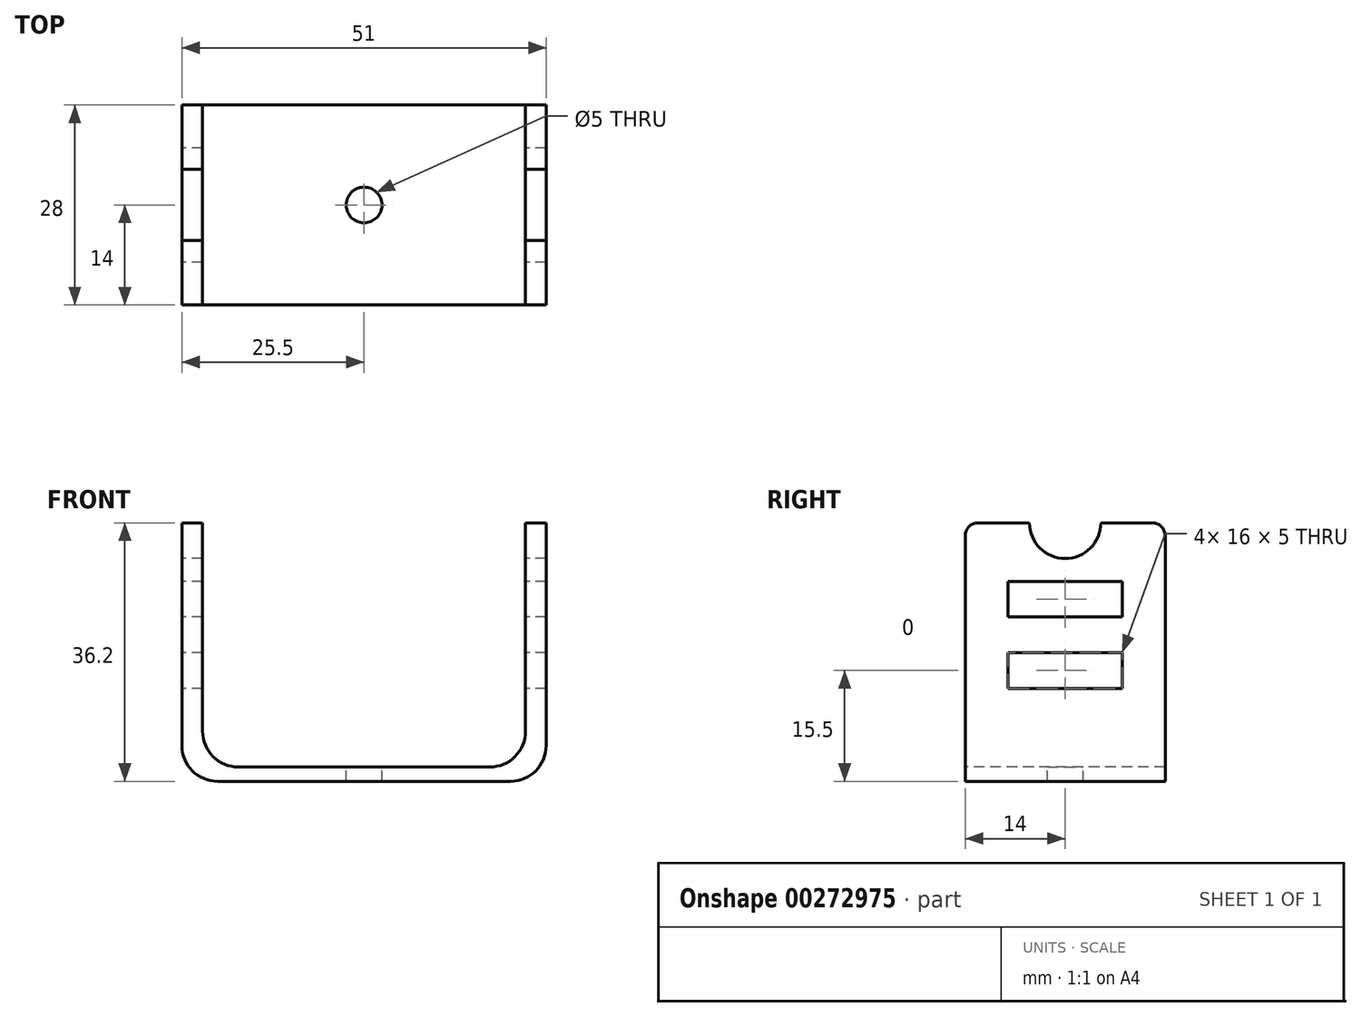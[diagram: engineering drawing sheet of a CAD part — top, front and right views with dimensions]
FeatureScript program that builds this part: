
annotation { "Feature Type Name" : "Feature", "Feature Type Description" : "" }
export const myFeature = defineFeature(function(context is Context, id is Id, definition is map)
    precondition{}
    {
        {
            var Q0;
            Q0=qCreatedBy(makeId("Right.planeOp"),FACE);
            var sketch = newSketch(context, id + "F0", { "sketchPlane" : qUnion([Q0])});
            skLineSegment(sketch, "E0.bottom", {"start": v(-14, 0) * mm, "end": v(14, 0) * mm});
            skLineSegment(sketch, "E0.top", {"start": v(-12.17, 36.2) * mm, "end": v(-5, 36.2) * mm});
            skLineSegment(sketch, "E0.left", {"start": v(-14, 0) * mm, "end": v(-14, 34.37) * mm});
            skLineSegment(sketch, "E0.right", {"start": v(14, 0) * mm, "end": v(14, 34.37) * mm});
            skLineSegment(sketch, "E1.bottom", {"start": v(-8, 18) * mm, "end": v(8, 18) * mm});
            skLineSegment(sketch, "E1.top", {"start": v(-8, 13) * mm, "end": v(8, 13) * mm});
            skLineSegment(sketch, "E1.left", {"start": v(-8, 18) * mm, "end": v(-8, 13) * mm});
            skLineSegment(sketch, "E1.right", {"start": v(8, 18) * mm, "end": v(8, 13) * mm});
            skLineSegment(sketch, "E2.0.1.0", {"start": v(-8, 23) * mm, "end": v(8, 23) * mm});
            skLineSegment(sketch, "E2.0.1.1", {"start": v(8, 28) * mm, "end": v(8, 23) * mm});
            skLineSegment(sketch, "E2.0.1.2", {"start": v(-8, 28) * mm, "end": v(8, 28) * mm});
            skLineSegment(sketch, "E2.0.1.3", {"start": v(-8, 28) * mm, "end": v(-8, 23) * mm});
            skLineSegment(sketch, "E2.direction1", {"start": v(-8, 13) * mm, "end": v(17, 13) * mm, "construction": true});
            skLineSegment(sketch, "E2.direction2", {"start": v(-8, 13) * mm, "end": v(-8, 23) * mm, "construction": true});
            skArc(sketch, "E3", {"start": v(-5, 36.2) * mm, "mid": v(0, 31.2) * mm, "end": v(5, 36.2) * mm});
            skLineSegment(sketch, "E4.trimOffspring", {"start": v(5, 36.2) * mm, "end": v(12.17, 36.2) * mm});
            skPoint(sketch, "E5.visualSharp", {"position": v(-14, 36.2) * mm});
            skArc(sketch, "E5.filletArc", {"start": v(-12.17, 36.2) * mm, "mid": v(-13.46, 35.66) * mm, "end": v(-14, 34.37) * mm});
            skPoint(sketch, "E6.visualSharp", {"position": v(14, 36.2) * mm});
            skArc(sketch, "E6.filletArc", {"start": v(14, 34.37) * mm, "mid": v(13.46, 35.66) * mm, "end": v(12.17, 36.2) * mm});
            skSolve(sketch);
        }
        {
            var Q0;
            Q0=makeQuery(id+"F0.imprint","IMPRINT",FACE,{"disambiguationData":[TD([[makeQuery(id+"F0.imprint","IMPRINT",EDGE,{"derivedFrom":sQuery(id+"F0.wireOp",EDGE,"E0.bottom")}),1.0]])]});
            extrude(context, id + "F1", {"entities" : qUnion([Q0]), "endBound" : BoundingType.SYMMETRIC, "depth" : 51 * mm});
        }
        {
            var Q0;
            Q0=makeQuery(id+"F1.opExtrude","SWEPT_FACE",FACE,{"disambiguationData":[OSD([sQuery(id+"F0.wireOp",EDGE,"E0.top")])]});
            var sketch = newSketch(context, id + "F2", { "sketchPlane" : qUnion([Q0])});
            skLineSegment(sketch, "E7.bottom", {"start": v(-22.6, 21.8) * mm, "end": v(22.6, 21.8) * mm});
            skLineSegment(sketch, "E7.top", {"start": v(-22.6, -21.02) * mm, "end": v(22.6, -21.02) * mm});
            skLineSegment(sketch, "E7.left", {"start": v(-22.6, 21.8) * mm, "end": v(-22.6, -21.02) * mm});
            skLineSegment(sketch, "E7.right", {"start": v(22.6, 21.8) * mm, "end": v(22.6, -21.02) * mm});
            skSolve(sketch);
        }
        {
            var Q0;
            Q0=qSketchRegion(id+"F2",true);
            extrude(context, id + "F3", {"entities" : qUnion([Q0]), "operationType" : NewBodyOperationType.REMOVE, "oppositeDirection" : true, "depth" : 34.2 * mm});
        }
        {
            var Q0;
            Q0=makeQuery(id+"F3.boolean.opBoolean","COPY",FACE,{"derivedFrom":makeQuery(id+"F3.opExtrude","CAP_FACE",FACE,{"disambiguationData":[OSD([sQuery(id+"F2.wireOp",EDGE,"E7.bottom"),sQuery(id+"F2.wireOp",EDGE,"E7.top"),sQuery(id+"F2.wireOp",EDGE,"E7.left"),sQuery(id+"F2.wireOp",EDGE,"E7.right")])],"isStart":false})});
            var sketch = newSketch(context, id + "F4", { "sketchPlane" : qUnion([Q0])});
            skCircle(sketch, "E8", {"center": v(0, 0) * mm, "radius": 2.5 * mm});
            skSolve(sketch);
        }
        {
            var Q0;
            Q0=qSketchRegion(id+"F4",true);
            extrude(context, id + "F5", {"entities" : qUnion([Q0]), "operationType" : NewBodyOperationType.REMOVE, "endBound" : BoundingType.THROUGH_ALL, "oppositeDirection" : true, "depth" : 25 * mm});
        }
        {
            var Q0;
            Q0=makeQuery(id+"F1.opExtrude","CAP_EDGE",EDGE,{"disambiguationData":[OSD([sQuery(id+"F0.wireOp",EDGE,"E0.bottom")])],"isStart":false});
            var Q1;
            Q1=makeQuery(id+"F3.boolean.opBoolean","COPY",EDGE,{"derivedFrom":makeQuery(id+"F3.opExtrude","CAP_EDGE",EDGE,{"disambiguationData":[OSD([sQuery(id+"F2.wireOp",EDGE,"E7.right")])],"isStart":false})});
            var Q2;
            Q2=makeQuery(id+"F3.boolean.opBoolean","COPY",EDGE,{"derivedFrom":makeQuery(id+"F3.opExtrude","CAP_EDGE",EDGE,{"disambiguationData":[OSD([sQuery(id+"F2.wireOp",EDGE,"E7.left")])],"isStart":false})});
            var Q3;
            Q3=makeQuery(id+"F1.opExtrude","CAP_EDGE",EDGE,{"disambiguationData":[OSD([sQuery(id+"F0.wireOp",EDGE,"E0.bottom")])],"isStart":true});
            fillet(context, id + "F6", {"entities" : qUnion([Q0, Q1, Q2, Q3]), "radius" : 5 * mm, "tangentPropagation" : true, "allowEdgeOverflow" : false});
        }
    });
